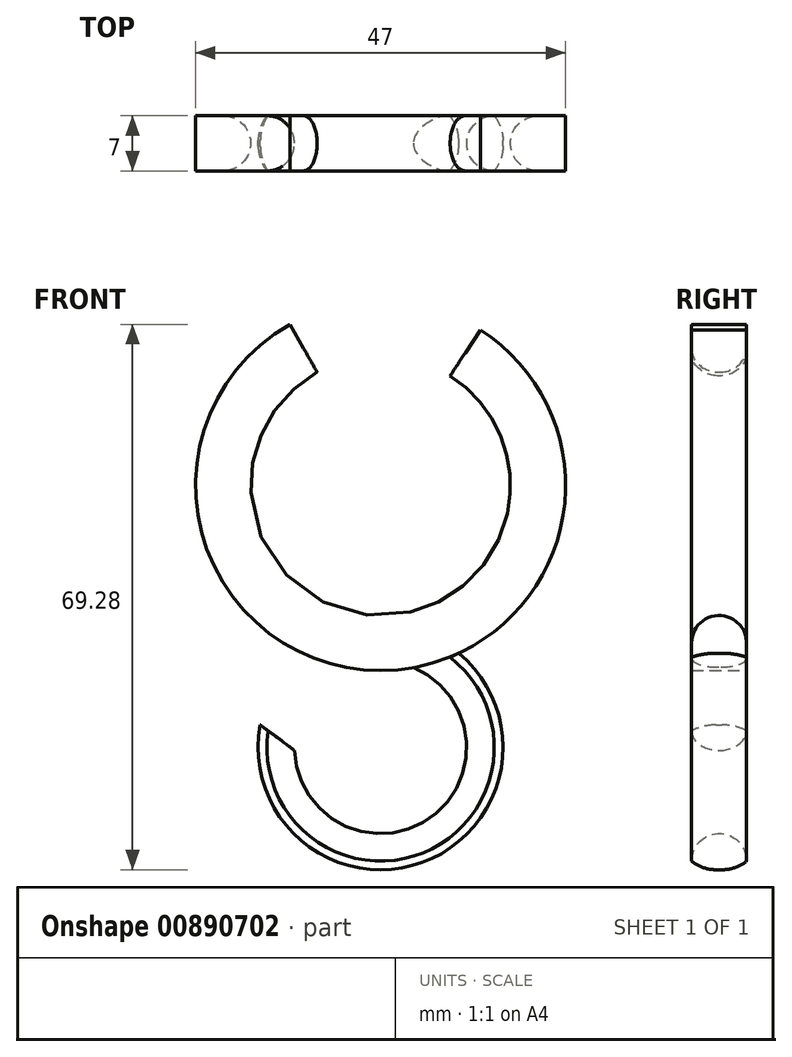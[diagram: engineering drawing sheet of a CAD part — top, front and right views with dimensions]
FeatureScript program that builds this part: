
annotation { "Feature Type Name" : "Feature", "Feature Type Description" : "" }
export const myFeature = defineFeature(function(context is Context, id is Id, definition is map)
    precondition{}
    {
        {
            var Q0;
            Q0=qCreatedBy(makeId("Front.planeOp"),FACE);
            var sketch = newSketch(context, id + "F0", { "sketchPlane" : qUnion([Q0])});
            skArc(sketch, "E0", {"start": v(12.69, 19.78) * mm, "mid": v(-0.68, -23.5) * mm, "end": v(-11.53, 20.48) * mm});
            skArc(sketch, "E1", {"start": v(8.83, 13.94) * mm, "mid": v(-0.46, -16.5) * mm, "end": v(-8.04, 14.4) * mm});
            skLineSegment(sketch, "E2", {"start": v(-11.53, 20.48) * mm, "end": v(-8.04, 14.4) * mm});
            skLineSegment(sketch, "E3", {"start": v(8.83, 13.94) * mm, "end": v(12.69, 19.78) * mm});
            skArc(sketch, "E4", {"start": v(4.15, -23.13) * mm, "mid": v(6.26, -42.24) * mm, "end": v(-10.94, -33.64) * mm});
            skArc(sketch, "E5", {"start": v(9.93, -21.3) * mm, "mid": v(5.28, -47.88) * mm, "end": v(-15.28, -30.4) * mm});
            skLineSegment(sketch, "E6", {"start": v(-15.28, -30.4) * mm, "end": v(-10.94, -33.64) * mm});
            skSolve(sketch);
        }
        {
            var Q0;
            Q0 = qSketchRegion(id + "F0", true);
            var Q1;
            Q1=makeQuery(id+"F0.imprint","IMPRINT",FACE,{"disambiguationData":[TD([[makeQuery(id+"F0.imprint","IMPRINT",EDGE,{"derivedFrom":sQuery(id+"F0.wireOp",EDGE,"E1")}),1.0]])]});
            extrude(context, id + "F1", {"entities" : qUnion([Q0, Q1]), "depth" : 7 * mm, "offsetDistance" : 25 * mm});
        }
        {
            var Q0;
            {var subQ0=sQuery(id+"F0.wireOp",EDGE,"E0");Q0=makeQuery(id+"F1.opExtrude","CAP_EDGE",EDGE,{"disambiguationData":[OSD([subQ0]),TDD([makeQuery(id+"F0.imprint","IMPRINT",EDGE,{"disambiguationData":[TD([[makeQuery(id+"F0.imprint","INTERSECT",VERTEX,{"derivedFrom":[subQ0,sQuery(id+"F0.wireOp",EDGE,"E3")]}),-1.0]])],"derivedFrom":subQ0})])],"isStart":true});}
            var Q1;
            {var subQ0=sQuery(id+"F0.wireOp",EDGE,"E0");Q1=makeQuery(id+"F1.opExtrude","CAP_EDGE",EDGE,{"disambiguationData":[OSD([subQ0]),TDD([makeQuery(id+"F0.imprint","IMPRINT",EDGE,{"disambiguationData":[TD([[makeQuery(id+"F0.imprint","INTERSECT",VERTEX,{"derivedFrom":[subQ0,sQuery(id+"F0.wireOp",EDGE,"E3")]}),-1.0]])],"derivedFrom":subQ0})])],"isStart":false});}
            var Q2;
            Q2=makeQuery(id+"F1.opExtrude","CAP_EDGE",EDGE,{"disambiguationData":[OSD([sQuery(id+"F0.wireOp",EDGE,"E1")])],"isStart":false});
            var Q3;
            Q3=makeQuery(id+"F1.opExtrude","CAP_EDGE",EDGE,{"disambiguationData":[OSD([sQuery(id+"F0.wireOp",EDGE,"E1")])],"isStart":true});
            var Q4;
            Q4=makeQuery(id+"F1.opExtrude","CAP_EDGE",EDGE,{"disambiguationData":[OSD([sQuery(id+"F0.wireOp",EDGE,"E4")])],"isStart":true});
            var Q5;
            Q5=makeQuery(id+"F1.opExtrude","CAP_EDGE",EDGE,{"disambiguationData":[OSD([sQuery(id+"F0.wireOp",EDGE,"E4")])],"isStart":false});
            var Q6;
            {var subQ0=sQuery(id+"F0.wireOp",EDGE,"E0");Q6=makeQuery(id+"F1.opExtrude","CAP_EDGE",EDGE,{"disambiguationData":[OSD([subQ0]),TDD([makeQuery(id+"F0.imprint","IMPRINT",EDGE,{"disambiguationData":[TD([[makeQuery(id+"F0.imprint","INTERSECT",VERTEX,{"derivedFrom":[subQ0,sQuery(id+"F0.wireOp",EDGE,"E2")]}),1.0]])],"derivedFrom":subQ0})])],"isStart":false});}
            var Q7;
            {var subQ0=sQuery(id+"F0.wireOp",EDGE,"E0");Q7=makeQuery(id+"F1.opExtrude","CAP_EDGE",EDGE,{"disambiguationData":[OSD([subQ0]),TDD([makeQuery(id+"F0.imprint","IMPRINT",EDGE,{"disambiguationData":[TD([[makeQuery(id+"F0.imprint","INTERSECT",VERTEX,{"derivedFrom":[subQ0,sQuery(id+"F0.wireOp",EDGE,"E2")]}),1.0]])],"derivedFrom":subQ0})])],"isStart":true});}
            fillet(context, id + "F2", {"entities" : qUnion([Q0, Q1, Q2, Q3, Q4, Q5, Q6, Q7]), "radius" : 3.5 * mm, "tangentPropagation" : true, "allowEdgeOverflow" : false});
        }
        {
            var Q0;
            Q0=makeQuery(id+"F1.opExtrude","CAP_EDGE",EDGE,{"disambiguationData":[OSD([sQuery(id+"F0.wireOp",EDGE,"E5")])],"isStart":false});
            var Q1;
            Q1=makeQuery(id+"F1.opExtrude","CAP_EDGE",EDGE,{"disambiguationData":[OSD([sQuery(id+"F0.wireOp",EDGE,"E5")])],"isStart":true});
            fillet(context, id + "F3", {"entities" : qUnion([Q0, Q1]), "radius" : 5 * mm, "tangentPropagation" : true, "allowEdgeOverflow" : false});
        }
    });
